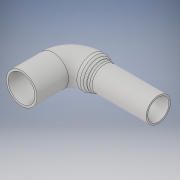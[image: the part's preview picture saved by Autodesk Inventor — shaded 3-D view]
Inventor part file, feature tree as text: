
AUTODESK INVENTOR PART (.ipt)
format: ipt  version: 2019 (Build 230136000, 136)  size: 308,736 bytes
history: native  units: mm
features: sketch x5, extrude x4, fillet x2, sweep x1
ambient origin geometry x8: Origin, YZ Plane, XZ Plane, XY Plane, X Axis, Y Axis, Z Axis, Center Point
bodies: Solid1 (feature_tree)
feature tree (12):
  extrude  "Extrusion1"  Depth=17.0mm
  extrude  "Extrusion2"  Depth=15.5mm
  extrude  "Extrusion3"  Depth=13.5mm
  sweep  "Sweep3"
  extrude  "Extrusion5"  Depth=15.5mm
  fillet  "Fillet6"  Radius=15.5mm
  fillet  "Fillet7"  Radius=13.5mm
  sketch  "Sketch1"  dims[d0=19.5mm d1=17.0mm]
  sketch  "Sketch2"  dims[d2=20.0mm d3=0.0mm d4=15.5mm]
  sketch  "Sketch3"  dims[d5=11.75mm d6=13.5mm]
  sketch  "Sketch10"  dims[d7=55.0mm d8=0.0mm d9=13.0mm d10=0.0mm]
  sketch  "Sketch13"  dims[d17=19.5mm d42=15.5mm d43=15.5mm d44=13.5mm d45=13.5mm d46=19.5mm d47=17.0mm d48=19.5mm d49=17.0mm d50=0.0mm d51=0.0mm d52=7.0mm d53=0.0mm d54=2.0mm d55=4.0mm]
